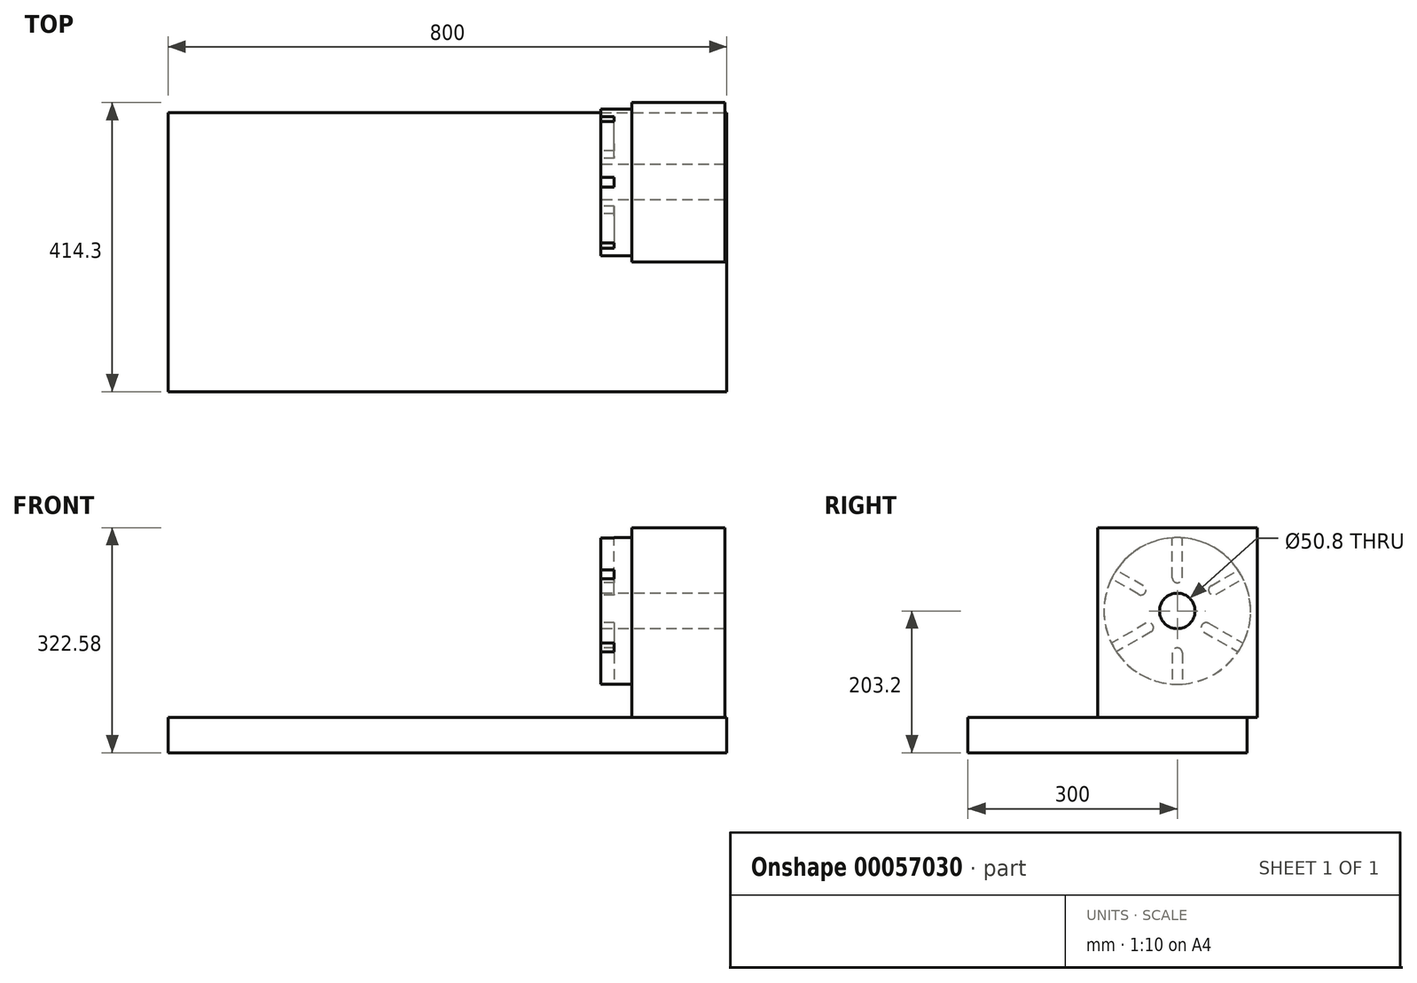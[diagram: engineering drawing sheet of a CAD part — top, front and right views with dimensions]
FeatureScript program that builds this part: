
annotation { "Feature Type Name" : "Feature", "Feature Type Description" : "" }
export const myFeature = defineFeature(function(context is Context, id is Id, definition is map)
    precondition{}
    {
        {
            var Q0;
            Q0=qCreatedBy(makeId("Top.planeOp"),FACE);
            var sketch = newSketch(context, id + "F0", { "sketchPlane" : qUnion([Q0])});
            skLineSegment(sketch, "E0.rect.bottom", {"start": v(-400, 200) * mm, "end": v(400, 200) * mm});
            skLineSegment(sketch, "E0.rect.top", {"start": v(-400, -200) * mm, "end": v(400, -200) * mm});
            skLineSegment(sketch, "E0.rect.left", {"start": v(-400, 200) * mm, "end": v(-400, -200) * mm});
            skLineSegment(sketch, "E0.rect.right", {"start": v(400, 200) * mm, "end": v(400, -200) * mm});
            skPoint(sketch, "E0.rect.middle", {"position": v(0, 0) * mm});
            skLineSegment(sketch, "E1.rect.bottom", {"start": v(350, 235.25) * mm, "end": v(-350, 235.25) * mm, "construction": true});
            skLineSegment(sketch, "E1.rect.top", {"start": v(350, -199.75) * mm, "end": v(-350, -199.75) * mm, "construction": true});
            skLineSegment(sketch, "E1.rect.left", {"start": v(350, 235.25) * mm, "end": v(350, -199.75) * mm, "construction": true});
            skLineSegment(sketch, "E1.rect.right", {"start": v(-350, 235.25) * mm, "end": v(-350, -199.75) * mm, "construction": true});
            skPoint(sketch, "E1.rect.middle", {"position": v(0, 17.75) * mm});
            skSolve(sketch);
        }
        {
            var Q0;
            Q0=makeQuery(id+"F0.imprint","IMPRINT",FACE,{"disambiguationData":[TD([[makeQuery(id+"F0.imprint","IMPRINT",EDGE,{"derivedFrom":sQuery(id+"F0.wireOp",EDGE,"E0.rect.bottom")}),-1.0]])]});
            extrude(context, id + "F1", {"entities" : qUnion([Q0]), "depth" : 50.8 * mm});
        }
        {
            var Q0;
            Q0=makeQuery(id+"F1.opExtrude","CAP_FACE",FACE,{"disambiguationData":[OSD([sQuery(id+"F0.wireOp",EDGE,"E0.rect.bottom"),sQuery(id+"F0.wireOp",EDGE,"E0.rect.top"),sQuery(id+"F0.wireOp",EDGE,"E0.rect.left"),sQuery(id+"F0.wireOp",EDGE,"E0.rect.right")])],"isStart":false});
            var sketch = newSketch(context, id + "F2", { "sketchPlane" : qUnion([Q0])});
            skLineSegment(sketch, "E2.bottom", {"start": v(264.11, 214.3) * mm, "end": v(397.46, 214.3) * mm});
            skLineSegment(sketch, "E2.top", {"start": v(264.11, -14.3) * mm, "end": v(397.46, -14.3) * mm});
            skLineSegment(sketch, "E2.left", {"start": v(264.11, 214.3) * mm, "end": v(264.11, -14.3) * mm});
            skLineSegment(sketch, "E2.right", {"start": v(397.46, 214.3) * mm, "end": v(397.46, -14.3) * mm});
            skSolve(sketch);
        }
        {
            var Q0;
            {var subQ6=sQuery(id+"F2.wireOp",EDGE,"E2.bottom");var subQ7=sQuery(id+"F2.wireOp",EDGE,"E2.top");Q0=qUnion([makeQuery(id+"F2.imprint","IMPRINT",FACE,{"disambiguationData":[TD([[makeQuery(id+"F2.imprint","IMPRINT",EDGE,{"derivedFrom":subQ6}),-1.0]])]}),makeQuery(id+"F2.imprint","IMPRINT",FACE,{"disambiguationData":[TD([[makeQuery(id+"F2.imprint","IMPRINT",EDGE,{"derivedFrom":subQ7}),1.0]])]})]);}
            extrude(context, id + "F3", {"entities" : qUnion([Q0]), "depth" : 271.78 * mm});
        }
        {
            var Q0;
            Q0=makeQuery(id+"F3.opExtrude","SWEPT_FACE",FACE,{"disambiguationData":[OSD([sQuery(id+"F2.wireOp",EDGE,"E2.left")])]});
            var sketch = newSketch(context, id + "F4", { "sketchPlane" : qUnion([Q0])});
            skCircle(sketch, "E3", {"center": v(-100, 203.2) * mm, "radius": 105 * mm});
            skPoint(sketch, "E4", {"position": v(-100, 50.8) * mm});
            skSolve(sketch);
        }
        {
            var Q0;
            Q0=makeQuery(id+"F4.imprint","IMPRINT",FACE,{"disambiguationData":[TD([[makeQuery(id+"F4.imprint","IMPRINT",EDGE,{"derivedFrom":sQuery(id+"F4.wireOp",EDGE,"E3")}),1.0]])]});
            extrude(context, id + "F5", {"entities" : qUnion([Q0]), "operationType" : NewBodyOperationType.ADD, "depth" : 44.45 * mm});
        }
        {
            var Q0;
            Q0=makeQuery(id+"F5.opExtrude","CAP_FACE",FACE,{"disambiguationData":[OSD([sQuery(id+"F4.wireOp",EDGE,"E3")])],"isStart":false});
            var sketch = newSketch(context, id + "F6", { "sketchPlane" : qUnion([Q0])});
            skArc(sketch, "E5", {"start": v(-107.14, 250.83) * mm, "mid": v(-100, 243.69) * mm, "end": v(-92.86, 250.83) * mm});
            skArc(sketch, "E6", {"start": v(-92.86, 143.13) * mm, "mid": v(-100, 150.27) * mm, "end": v(-107.14, 143.13) * mm});
            skCircle(sketch, "E7", {"center": v(-100, 203.2) * mm, "radius": 60.07 * mm, "construction": true});
            skCircle(sketch, "E8", {"center": v(-100, 203.2) * mm, "radius": 47.63 * mm, "construction": true});
            skLineSegment(sketch, "E9", {"start": v(-107.14, 250.29) * mm, "end": v(-107.14, 308.2) * mm});
            skLineSegment(sketch, "E10", {"start": v(-92.86, 250.29) * mm, "end": v(-92.86, 308.2) * mm});
            skLineSegment(sketch, "E11", {"start": v(-92.86, 143.55) * mm, "end": v(-92.86, 98.2) * mm});
            skLineSegment(sketch, "E12", {"start": v(-107.14, 143.55) * mm, "end": v(-107.14, 98.2) * mm});
            skArc(sketch, "E13", {"start": v(-92.86, 308.2) * mm, "mid": v(-100, 315.34) * mm, "end": v(-107.14, 308.2) * mm});
            skArc(sketch, "E14", {"start": v(-107.14, 98.2) * mm, "mid": v(-100, 91.06) * mm, "end": v(-92.86, 98.2) * mm});
            skLineSegment(sketch, "E15.1.0", {"start": v(-144.35, 185.84) * mm, "end": v(-194.5, 156.88) * mm});
            skArc(sketch, "E15.1.1", {"start": v(-194.5, 156.88) * mm, "mid": v(-197.11, 147.13) * mm, "end": v(-187.36, 144.52) * mm});
            skLineSegment(sketch, "E15.1.2", {"start": v(-137.2, 173.48) * mm, "end": v(-187.36, 144.52) * mm});
            skArc(sketch, "E15.1.3", {"start": v(-137.68, 173.2) * mm, "mid": v(-135.06, 182.96) * mm, "end": v(-144.81, 185.57) * mm});
            skLineSegment(sketch, "E15.2.0", {"start": v(-62.8, 173.48) * mm, "end": v(-12.64, 144.52) * mm});
            skArc(sketch, "E15.2.1", {"start": v(-12.64, 144.52) * mm, "mid": v(-2.89, 147.13) * mm, "end": v(-5.5, 156.88) * mm});
            skLineSegment(sketch, "E15.2.2", {"start": v(-55.65, 185.84) * mm, "end": v(-5.5, 156.88) * mm});
            skArc(sketch, "E15.2.3", {"start": v(-55.19, 185.57) * mm, "mid": v(-64.94, 182.96) * mm, "end": v(-62.32, 173.2) * mm});
            skLineSegment(sketch, "E16.1.0", {"start": v(-44.78, 226.84) * mm, "end": v(-5.5, 249.52) * mm});
            skArc(sketch, "E16.1.1", {"start": v(-51.55, 239.42) * mm, "mid": v(-54.16, 229.67) * mm, "end": v(-44.4, 227.05) * mm});
            skLineSegment(sketch, "E16.1.2", {"start": v(-51.91, 239.2) * mm, "end": v(-12.64, 261.88) * mm});
            skArc(sketch, "E16.1.3", {"start": v(-5.5, 249.52) * mm, "mid": v(-2.89, 259.27) * mm, "end": v(-12.64, 261.88) * mm});
            skLineSegment(sketch, "E16.2.0", {"start": v(-148.09, 239.2) * mm, "end": v(-187.36, 261.88) * mm});
            skArc(sketch, "E16.2.1", {"start": v(-155.6, 227.05) * mm, "mid": v(-145.84, 229.67) * mm, "end": v(-148.45, 239.42) * mm});
            skLineSegment(sketch, "E16.2.2", {"start": v(-155.22, 226.84) * mm, "end": v(-194.5, 249.52) * mm});
            skArc(sketch, "E16.2.3", {"start": v(-187.36, 261.88) * mm, "mid": v(-197.11, 259.27) * mm, "end": v(-194.5, 249.52) * mm});
            skSolve(sketch);
        }
        {
            var Q0;
            Q0=qSketchRegion(id+"F6",true);
            extrude(context, id + "F7", {"entities" : qUnion([Q0]), "operationType" : NewBodyOperationType.REMOVE, "oppositeDirection" : true, "depth" : 19.3 * mm});
        }
        {
            var Q0;
            Q0=makeQuery(id+"F5.opExtrude","CAP_FACE",FACE,{"disambiguationData":[OSD([sQuery(id+"F4.wireOp",EDGE,"E3")])],"isStart":false});
            var sketch = newSketch(context, id + "F8", { "sketchPlane" : qUnion([Q0])});
            skCircle(sketch, "E17", {"center": v(-100, 203.2) * mm, "radius": 25.4 * mm});
            skSolve(sketch);
        }
        {
            var Q0;
            Q0=makeQuery(id+"F8.imprint","IMPRINT",FACE,{"disambiguationData":[TD([[makeQuery(id+"F8.imprint","IMPRINT",EDGE,{"derivedFrom":sQuery(id+"F8.wireOp",EDGE,"E17")}),1.0]])]});
            extrude(context, id + "F9", {"entities" : qUnion([Q0]), "operationType" : NewBodyOperationType.REMOVE, "endBound" : BoundingType.THROUGH_ALL, "oppositeDirection" : true, "depth" : 25.4 * mm});
        }
    });
